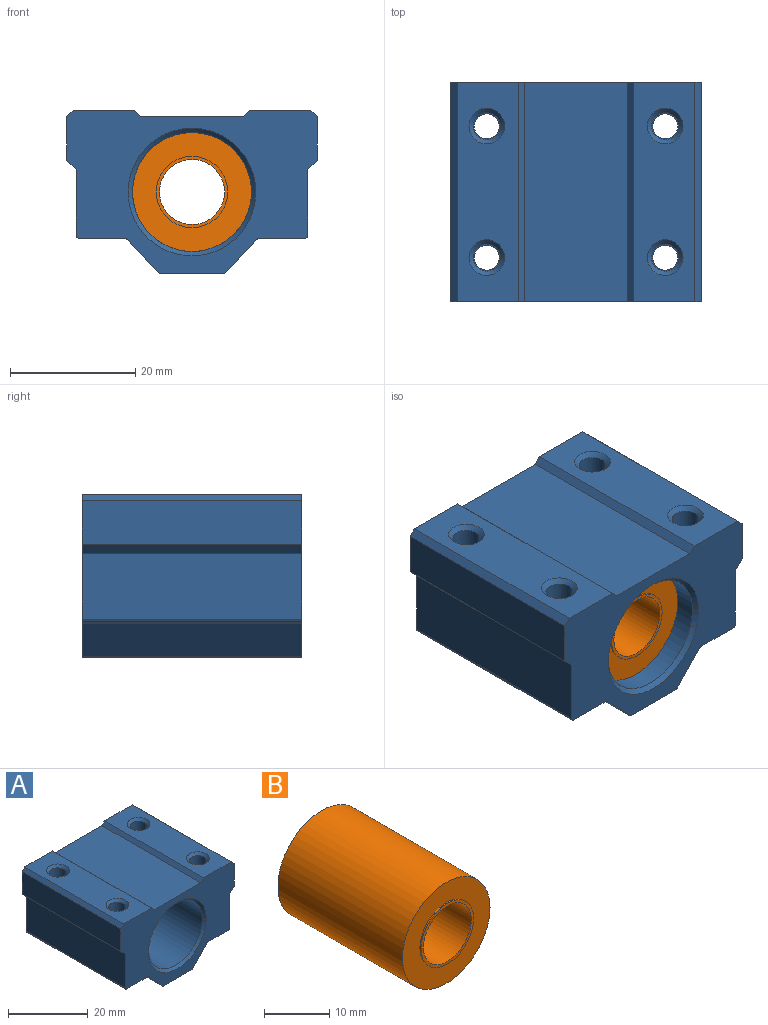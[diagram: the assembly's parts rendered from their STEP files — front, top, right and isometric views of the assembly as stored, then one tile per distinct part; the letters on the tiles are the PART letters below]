
ASSEMBLY  parts=2 mates=1
PART A: 45 faces, bbox 40x35x26 mm
  f0: cylinder r=9.5mm len=33.6mm, axis (0,1,0), area 2005.6mm2, adj f22,f23
  f1: plane 35x10.07mm, normal (0,0,-1), area 352.3mm2, adj f8,f9,f13,f34
  f2: plane 35x5.28mm, normal (0.73,0,-0.68), area 253.5mm2, adj f8,f9,f13,f14
  f3: plane 35x7.28mm, normal (0,0,-1), area 229.8mm2, adj f8,f9,f14,f15,f16,f19
  f4: plane 35x10.5mm, normal (1,0,0), area 367.5mm2, adj f8,f9,f12,f15
  f5: plane 35x6.9mm, normal (1,0,0), area 241.5mm2, adj f8,f9,f10,f12
  f6: plane 35x9.75mm, normal (0,0,1), area 290.2mm2, adj f8,f9,f10,f11,f24,f25
  f7: plane 35x16.5mm, normal (0,0,1), area 577.5mm2, adj f8,f9,f11,f32
  f8: plane 40x26mm, normal (0,-1,0), area 523.5mm2, adj f1,f2,f3,f4,f5,f6,f7,f10
  f9: plane 40x26mm, normal (0,1,0), area 523.5mm2, adj f1,f2,f3,f4,f5,f6,f7,f10
  f10: plane 35x1mm, normal (0.71,0,0.71), area 49.5mm2, adj f5,f6,f8,f9
  f11: plane 35x1mm, normal (-0.71,0,0.71), area 49.5mm2, adj f6,f7,f8,f9
  f12: plane 35x1.5mm, normal (0.71,0,-0.71), area 74.2mm2, adj f4,f5,f8,f9
  f13: cylinder r=0.5mm len=35mm, axis (0,1,0), area 14.3mm2, adj f1,f2,f8,f9
  f14: cylinder r=0.5mm len=35mm, axis (0,-1,0), area 14.3mm2, adj f2,f3,f8,f9
  f15: cylinder r=0.5mm len=35mm, axis (0,1,0), area 27.5mm2, adj f3,f4,f8,f9
  f16: cylinder r=2mm len=8.4mm, axis (0,0,1), area 105.6mm2, adj f3,f17
  f17: plane 4.3x4.3mm, normal (0,0,1), area 2mm2, adj f16,f18
  f18: cylinder r=2.15mm len=11.3mm, axis (0,0,1), area 152.6mm2, adj f17,f24
  f19: cylinder r=2mm len=8.4mm, axis (0,0,1), area 105.6mm2, adj f3,f20
  f20: plane 4.3x4.3mm, normal (0,0,1), area 2mm2, adj f19,f21
  f21: cylinder r=2.15mm len=11.3mm, axis (0,0,1), area 152.6mm2, adj f20,f25
  f22: cone r=10.2mm half-angle=45deg, axis (0,1,0), area 61.3mm2, adj f0,f9
  f23: cone r=9.5mm half-angle=45deg, axis (0,-1,0), area 61.3mm2, adj f0,f8
  f24: cone r=2.15mm half-angle=45deg, axis (0,0,1), area 15.6mm2, adj f6,f18
  f25: cone r=2.15mm half-angle=45deg, axis (0,0,1), area 15.6mm2, adj f6,f21
  f26: plane 35x5.28mm, normal (-0.73,0,-0.68), area 253.5mm2, adj f8,f9,f34,f35
  f27: plane 35x7.28mm, normal (0,0,-1), area 229.8mm2, adj f8,f9,f35,f36,f37,f40
  f28: plane 35x10.5mm, normal (-1,0,0), area 367.5mm2, adj f8,f9,f33,f36
  f29: plane 35x6.9mm, normal (-1,0,0), area 241.5mm2, adj f8,f9,f31,f33
  f30: plane 35x9.75mm, normal (0,0,1), area 290.2mm2, adj f8,f9,f31,f32,f43,f44
  f31: plane 35x1mm, normal (-0.71,0,0.71), area 49.5mm2, adj f8,f9,f29,f30
  f32: plane 35x1mm, normal (0.71,0,0.71), area 49.5mm2, adj f7,f8,f9,f30
  f33: plane 35x1.5mm, normal (-0.71,0,-0.71), area 74.2mm2, adj f8,f9,f28,f29
  f34: cylinder r=0.5mm len=35mm, axis (0,1,0), area 14.3mm2, adj f1,f8,f9,f26
  f35: cylinder r=0.5mm len=35mm, axis (0,-1,0), area 14.3mm2, adj f8,f9,f26,f27
  f36: cylinder r=0.5mm len=35mm, axis (0,1,0), area 27.5mm2, adj f8,f9,f27,f28
  f37: cylinder r=2mm len=8.4mm, axis (0,0,1), area 105.6mm2, adj f27,f38
  f38: plane 4.3x4.3mm, normal (0,0,1), area 2mm2, adj f37,f39
  f39: cylinder r=2.15mm len=11.3mm, axis (0,0,1), area 152.6mm2, adj f38,f43
  f40: cylinder r=2mm len=8.4mm, axis (0,0,1), area 105.6mm2, adj f27,f41
  f41: plane 4.3x4.3mm, normal (0,0,1), area 2mm2, adj f40,f42
  f42: cylinder r=2.15mm len=11.3mm, axis (0,0,1), area 152.6mm2, adj f41,f44
  f43: cone r=2.15mm half-angle=45deg, axis (0,0,1), area 15.6mm2, adj f30,f39
  f44: cone r=2.15mm half-angle=45deg, axis (0,0,1), area 15.6mm2, adj f30,f42
PART B: 8 faces, bbox 19x27.5x19 mm
  f0: cylinder r=9.5mm len=27mm, axis (0,1,0), area 1611.6mm2, adj f1,f2
  f1: plane 19x19mm, normal (0,-1,0), area 181.5mm2, adj f0,f3
  f2: plane 19x19mm, normal (0,1,0), area 181.5mm2, adj f0,f5
  f3: cylinder r=5.7mm len=11.4mm, axis (0,1,0), area 9mm2, adj f1,f6
  f4: cylinder r=5.2mm len=27.5mm, axis (0,1,0), area 898.5mm2, adj f6,f7
  f5: cylinder r=5.7mm len=11.4mm, axis (0,1,0), area 9mm2, adj f2,f7
  f6: plane 11.4x11.4mm, normal (0,-1,0), area 17.1mm2, adj f3,f4
  f7: plane 11.4x11.4mm, normal (0,1,0), area 17.1mm2, adj f4,f5
PLACE A at identity
PLACE B at identity
MATE fastened B.f0 <-> A.f0  axis (0,-1,0) through (0,-13.5,0)mm
